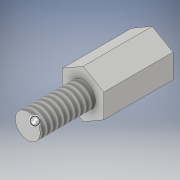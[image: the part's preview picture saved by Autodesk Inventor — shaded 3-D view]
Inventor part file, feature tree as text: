
AUTODESK INVENTOR PART (.ipt)
format: ipt  version: 2019 (Build 230136000, 136)  size: 138,240 bytes
history: native  units: mm
features: other x7, thread x2, extrude x2, hole x1, sketch x1
ambient origin geometry x8: Origin, YZ Plane, XZ Plane, XY Plane, X Axis, Y Axis, Z Axis, Center Point
bodies: Solid1 (feature_tree)
feature tree (13):
  other  "Spacer"
  other  "Table"
  thread  "Thread1:Designation = M2x0.4"  [1 undecoded]
  other  "d1 = 5 mm"
  other  "d1 = 10mm"
  other  "d1 = 15mm"
  other  "d1 = 20mm"
  other  "d1 = 25mm"
  extrude  "Hexagon1"  Depth=4.0mm TaperAngle=0.0deg
  hole  "Hole1"  [1 undecoded]
  extrude  "Extrusion2"  Depth=2.999912mm
  thread  "Thread3"  [1 undecoded]
  sketch  "Sketch1"  dims[d1=5.0mm d2=0.0mm d17=10.0mm d18=10.0mm d5=1.567mm d6=4.0mm d7=4.4mm d8=2.0mm d9=90.0deg d10=4.0mm d11=0.0mm d13=4.0mm d14=0.0mm d19=0.0mm d20=2.999912mm d21=1.732mm d22=1.8mm d25=10.0mm d26=0.0mm]
note: 3 required parameter values undecoded (feature->parameter linkage not recoverable at this tier; creation-order binding heuristic only, values carry confidence <= 0.55)
